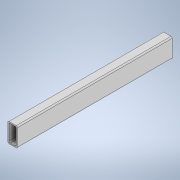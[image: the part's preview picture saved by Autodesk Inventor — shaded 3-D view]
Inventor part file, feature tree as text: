
AUTODESK INVENTOR PART (.ipt)
format: ipt  version: 2020 (Build 240168000, 168)  size: 119,296 bytes
history: native  units: in
note: dims shown in document units (in); Inventor stores cm internally (conversion verified against a paired STEP export)
features: extrude x1, sketch x1
ambient origin geometry x8: Origin, YZ Plane, XZ Plane, XY Plane, X Axis, Y Axis, Z Axis, Center Point
bodies: Solid1 (feature_tree)
feature tree (2):
  extrude  "Extrusion1"  Depth=1.0in
  sketch  "Sketch1"  dims[d0=2.0in d1=1.0in d2=0.125in d3=0.125in d4=0.125in d5=0.125in d6=0.125in d7=0.125in d8=0.125in d9=0.125in d10=0.125in d11=16.0in d12=0.0in]
